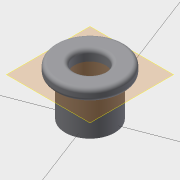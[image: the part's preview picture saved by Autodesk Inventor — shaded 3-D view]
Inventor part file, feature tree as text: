
AUTODESK INVENTOR PART (.ipt)
format: ipt  version: 2014 (Build 180170000, 170)  size: 206,336 bytes
history: native  units: mm
features: extrude x4, sketch x4, fillet x2, plane x1, chamfer x1, reference x1
ambient origin geometry x8: Origin, YZ Plane, XZ Plane, XY Plane, X Axis, Y Axis, Z Axis, Center Point
bodies: Solid1 (feature_tree)
feature tree (13):
  plane  "Work Plane1"
  extrude  "Extrusion1"  Depth=9.0mm
  extrude  "Extrusion2"  Depth=0.5mm
  fillet  "Fillet1"  Radius=0.3mm
  extrude  "Extrusion3"  Depth=1.5mm
  chamfer  "Chamfer1"  Distance=1.0mm
  fillet  "Fillet2"  Radius=10.0mm
  extrude  "Extrusion4"  Depth=1.0mm
  sketch  "Sketch1"  dims[d0=5.0mm d1=0.0mm d2=9.0mm]
  reference  "Reference1"
  sketch  "Sketch2"  dims[d3=1.5mm d4=0.0mm d5=0.5mm d6=0.3mm]
  sketch  "Sketch3"  dims[d7=2.0mm d8=0.0mm d9=1.5mm d10=2.0mm d11=3.490659mm]
  sketch  "Sketch4"  dims[d12=0.5mm d13=1.0mm d14=10.0mm d15=1.0mm d16=5.0mm d17=0.0mm]
